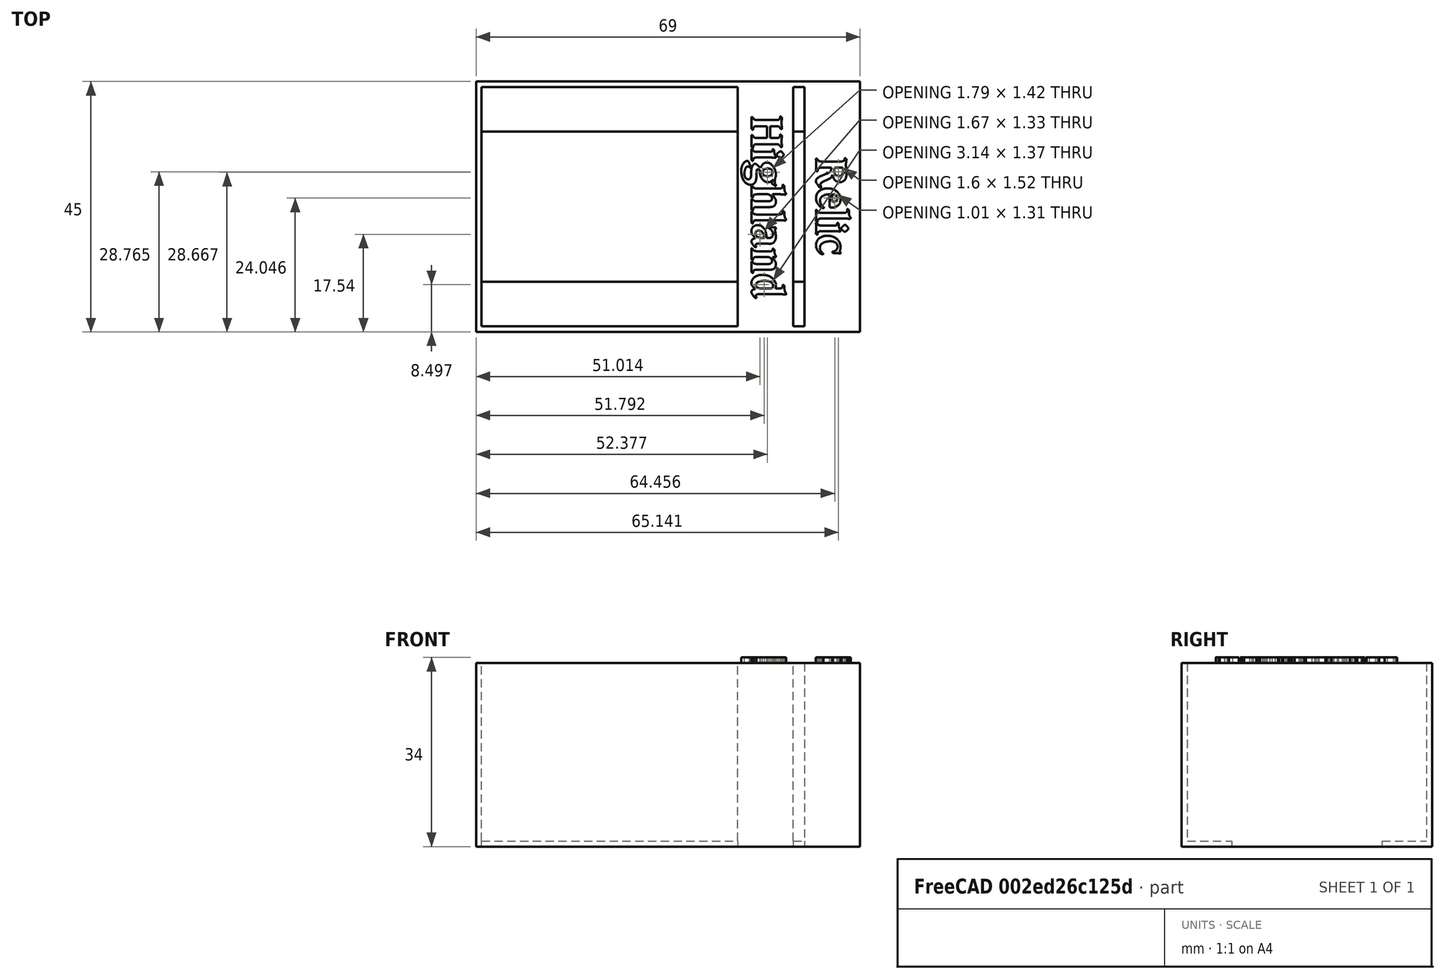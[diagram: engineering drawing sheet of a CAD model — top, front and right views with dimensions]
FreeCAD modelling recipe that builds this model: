
FCSTD DOCUMENT  (FreeCAD 0.18R4 (GitTag))
Label: highlands
License: All rights reserved
LicenseURL: http://en.wikipedia.org/wiki/All_rights_reserved
objects: Part::Box×8, Part::MultiFuse×4, Part::Cut×2, Part::Part2DObjectPython×2, Part::Extrusion×2
note: 18 computed .brp shape members not serialized (recipe doc carries the construction recipe); baked Part::Feature solids carry a one-line shape summary decoded from their .brp

FEATURE [Part::Box] Box  label="Cube"
  AttacherType = Attacher::AttachEngine3D
  Height = 33
  Length = 202
  Placement = pos=(0,-1,0) rot=(0,0,1;0rad)
  Width = 45
FEATURE [Part::Box] Box001  label="Cube001"
  AttacherType = Attacher::AttachEngine3D
  Height = 33
  Length = 200
  Placement = pos=(1,0,0) rot=(0,0,1;0rad)
  Width = 43
FEATURE [Part::Cut] Cut
  Base = -> Box
  Tool = -> Box001
FEATURE [Part::Box] Box002  label="Cube002"
  AttacherType = Attacher::AttachEngine3D
  Height = 1
  Length = 202
  Width = 8
FEATURE [Part::Box] Box003  label="Cube003"
  AttacherType = Attacher::AttachEngine3D
  Height = 1
  Length = 202
  Placement = pos=(0,35,0) rot=(0,0,1;0rad)
  Width = 8
FEATURE [Part::MultiFuse] Fusion
  Shapes = -> [Cut,Box002,Box003]
FEATURE [Part::Box] Box004  label="Cube004"
  AttacherType = Attacher::AttachEngine3D
  Height = 33
  Length = 10
  Placement = pos=(47,0,0) rot=(0,0,1;0rad)
  Width = 43
FEATURE [Part::Box] Box005  label="Cube005"
  AttacherType = Attacher::AttachEngine3D
  Height = 33
  Length = 10
  Placement = pos=(60,0,0) rot=(0,0,1;0rad)
  Width = 43
FEATURE [Part::Box] Box006  label="Cube006"
  AttacherType = Attacher::AttachEngine3D
  Height = 33
  Length = 141
  Placement = pos=(61,-1,0) rot=(0,0,1;0rad)
  Width = 45
FEATURE [Part::MultiFuse] Fusion001
  Shapes = -> [Fusion,Box004,Box005]
FEATURE [Part::Cut] Cut001
  Base = -> Fusion001
  Tool = -> Box006
FEATURE [Part::Box] Box007  label="Cube007"
  AttacherType = Attacher::AttachEngine3D
  Height = 33
  Length = 10
  Placement = pos=(59,-1,0) rot=(0,0,1;0rad)
  Width = 45
FEATURE [Part::MultiFuse] Fusion002
  Shapes = -> [Cut001,Box007]
FEATURE [Part::Part2DObjectPython] ShapeString  # Draft 2D object (typed FeaturePython)
  FontFile = <userpath>/Downloads/talisman/Caxton Bold.otf
  Placement = pos=(50.19,26.13,33) rot=(0,0,1;0rad)
  Size = 3
  String = Highland
  Tracking = 0
FEATURE [Part::Part2DObjectPython] ShapeString001  # Draft 2D object (typed FeaturePython)
  FontFile = <userpath>/Downloads/talisman/Caxton Bold.otf
  Placement = pos=(52.65,7.23,33) rot=(0,0,1;0rad)
  Size = 3
  String = Relic
  Tracking = 0
FEATURE [Part::Extrusion] Extrude
  Base = -> ShapeString
  Dir = (0,0,1)
  DirMode = 2
  FaceMakerClass = Part::FaceMakerBullseye
  LengthFwd = 1
  LengthRev = 0
  Placement = pos=(23.5,88,0) rot=(0,0,-1;1.5708rad)
  Solid = false
  Symmetric = false
FEATURE [Part::Extrusion] Extrude001
  Base = -> ShapeString001
  Dir = (0,0,1)
  DirMode = 2
  FaceMakerClass = Part::FaceMakerBullseye
  LengthFwd = 1
  LengthRev = 0
  Placement = pos=(54,83,0) rot=(0,0,-1;1.5708rad)
  Solid = false
  Symmetric = false
FEATURE [Part::MultiFuse] Fusion003
  Shapes = -> [Extrude,Extrude001]
